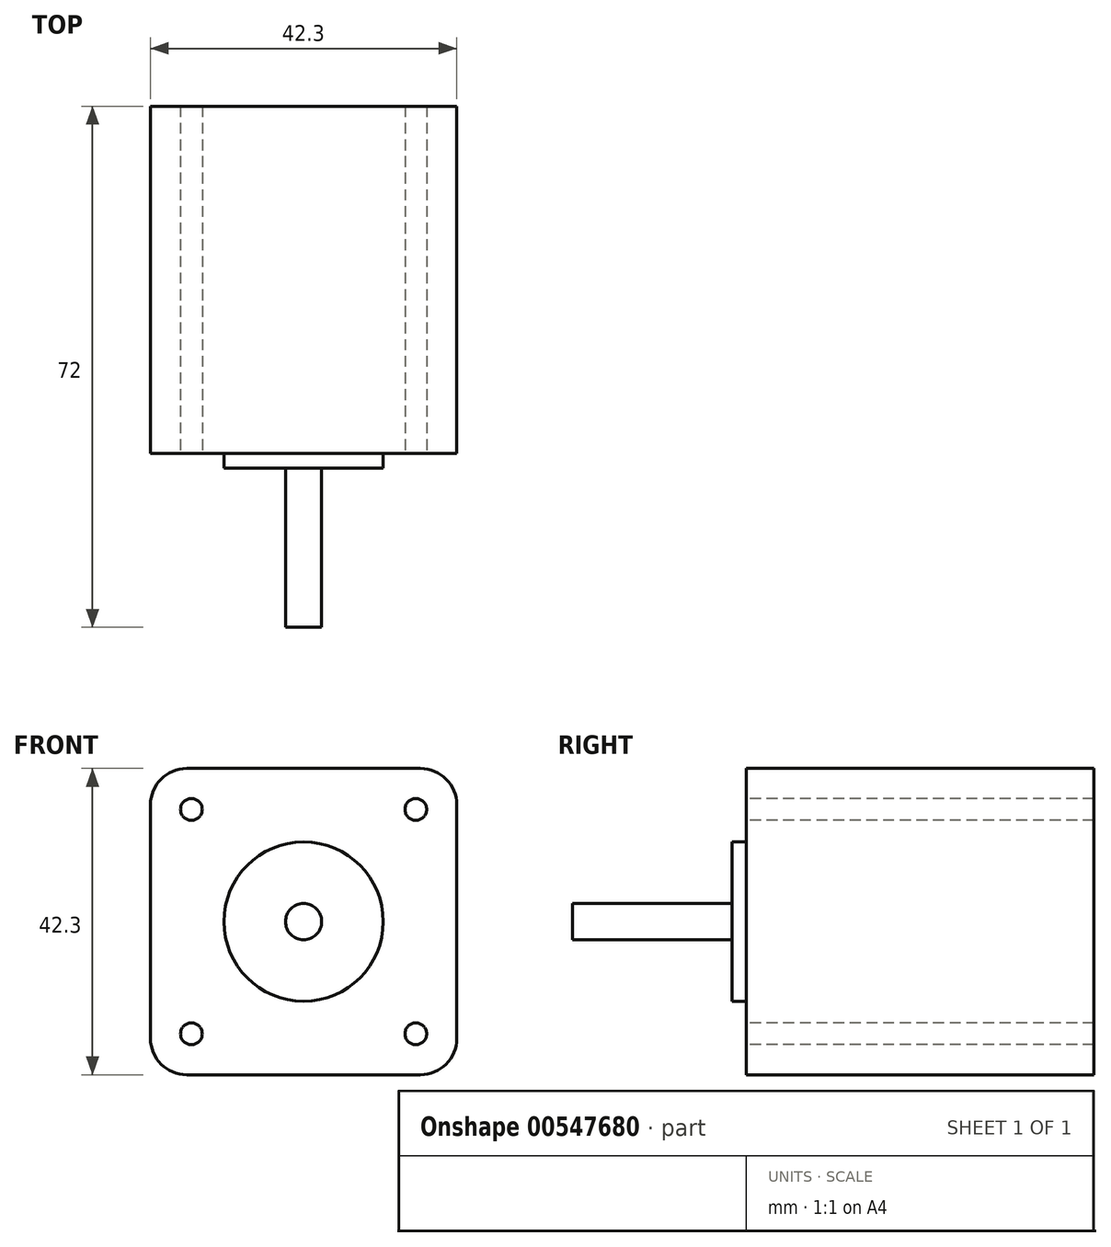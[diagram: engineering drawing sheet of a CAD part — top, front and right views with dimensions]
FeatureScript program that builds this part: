
annotation { "Feature Type Name" : "Feature", "Feature Type Description" : "" }
export const myFeature = defineFeature(function(context is Context, id is Id, definition is map)
    precondition{}
    {
        {
            var Q0;
            Q0=qCreatedBy(makeId("Front.planeOp"),FACE);
            var sketch = newSketch(context, id + "F0", { "sketchPlane" : qUnion([Q0])});
            skCircle(sketch, "E0", {"center": v(0, 0) * mm, "radius": 11 * mm});
            skCircle(sketch, "E1", {"center": v(0, 0) * mm, "radius": 2.5 * mm});
            skLineSegment(sketch, "E2.bottom", {"start": v(21.15, 21.15) * mm, "end": v(-21.15, 21.15) * mm});
            skLineSegment(sketch, "E2.top", {"start": v(21.15, -21.15) * mm, "end": v(-21.15, -21.15) * mm});
            skLineSegment(sketch, "E2.left", {"start": v(21.15, 21.15) * mm, "end": v(21.15, -21.15) * mm});
            skLineSegment(sketch, "E2.right", {"start": v(-21.15, 21.15) * mm, "end": v(-21.15, -21.15) * mm});
            skCircle(sketch, "E3", {"center": v(15.5, 15.5) * mm, "radius": 1.5 * mm});
            skLineSegment(sketch, "E4", {"start": v(0, 21.15) * mm, "end": v(0, -21.15) * mm, "construction": true});
            skLineSegment(sketch, "E5", {"start": v(21.15, 0) * mm, "end": v(-21.15, 0) * mm, "construction": true});
            skCircle(sketch, "E6.MirrorC", {"center": v(-15.5, 15.5) * mm, "radius": 1.5 * mm});
            skCircle(sketch, "E7.MirrorC", {"center": v(-15.5, -15.5) * mm, "radius": 1.5 * mm});
            skCircle(sketch, "E8.MirrorC", {"center": v(15.5, -15.5) * mm, "radius": 1.5 * mm});
            skSolve(sketch);
        }
        {
            var Q0;
            Q0=makeQuery(id+"F0.imprint","IMPRINT",FACE,{"disambiguationData":[TD([[makeQuery(id+"F0.imprint","IMPRINT",EDGE,{"derivedFrom":sQuery(id+"F0.wireOp",EDGE,"E1")}),1.0]])]});
            extrude(context, id + "F1", {"entities" : qUnion([Q0]), "depth" : 24 * mm});
        }
        {
            var Q0;
            Q0=makeQuery(id+"F0.imprint","IMPRINT",FACE,{"disambiguationData":[TD([[makeQuery(id+"F0.imprint","IMPRINT",EDGE,{"derivedFrom":sQuery(id+"F0.wireOp",EDGE,"E0")}),1.0]])]});
            extrude(context, id + "F2", {"entities" : qUnion([Q0]), "operationType" : NewBodyOperationType.ADD, "depth" : 2 * mm});
        }
        {
            var Q0;
            Q0=makeQuery(id+"F0.imprint","IMPRINT",FACE,{"disambiguationData":[TD([[makeQuery(id+"F0.imprint","IMPRINT",EDGE,{"derivedFrom":sQuery(id+"F0.wireOp",EDGE,"E1")}),1.0]])]});
            var Q1;
            Q1=makeQuery(id+"F0.imprint","IMPRINT",FACE,{"disambiguationData":[TD([[makeQuery(id+"F0.imprint","IMPRINT",EDGE,{"derivedFrom":sQuery(id+"F0.wireOp",EDGE,"E0")}),1.0]])]});
            var Q2;
            Q2=makeQuery(id+"F0.imprint","IMPRINT",FACE,{"disambiguationData":[TD([[makeQuery(id+"F0.imprint","IMPRINT",EDGE,{"derivedFrom":sQuery(id+"F0.wireOp",EDGE,"E0")}),-1.0]])]});
            extrude(context, id + "F3", {"entities" : qUnion([Q0, Q1, Q2]), "operationType" : NewBodyOperationType.ADD, "oppositeDirection" : true, "depth" : 48 * mm});
        }
        {
            var Q0;
            Q0=makeQuery(id+"F3.opExtrude","SWEPT_EDGE",EDGE,{"disambiguationData":[OSD([sQuery(id+"F0.wireOp",EDGE,"E2.bottom"),sQuery(id+"F0.wireOp",EDGE,"E2.left")])]});
            var Q1;
            Q1=makeQuery(id+"F3.opExtrude","SWEPT_EDGE",EDGE,{"disambiguationData":[OSD([sQuery(id+"F0.wireOp",EDGE,"E2.top"),sQuery(id+"F0.wireOp",EDGE,"E2.left")])]});
            var Q2;
            Q2=makeQuery(id+"F3.opExtrude","SWEPT_EDGE",EDGE,{"disambiguationData":[OSD([sQuery(id+"F0.wireOp",EDGE,"E2.top"),sQuery(id+"F0.wireOp",EDGE,"E2.right")])]});
            var Q3;
            Q3=makeQuery(id+"F3.opExtrude","SWEPT_EDGE",EDGE,{"disambiguationData":[OSD([sQuery(id+"F0.wireOp",EDGE,"E2.bottom"),sQuery(id+"F0.wireOp",EDGE,"E2.right")])]});
            fillet(context, id + "F4", {"entities" : qUnion([Q0, Q1, Q2, Q3]), "radius" : 5 * mm, "tangentPropagation" : true, "allowEdgeOverflow" : false});
        }
    });
